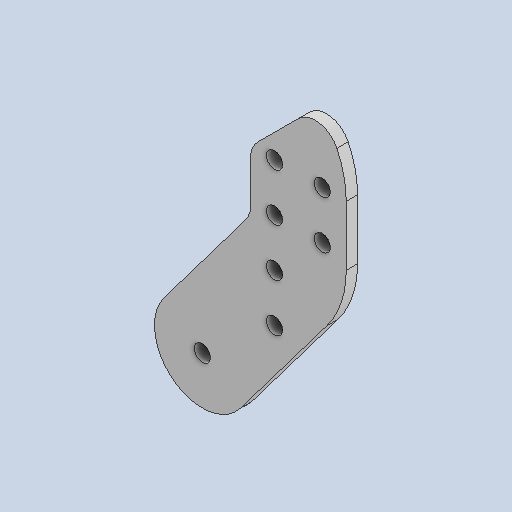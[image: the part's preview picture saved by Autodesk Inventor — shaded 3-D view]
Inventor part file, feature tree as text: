
AUTODESK INVENTOR PART (.ipt)
format: ipt  version: 2023 (Build 270158000, 158)  size: 117,248 bytes
history: native  units: in
note: dims shown in document units (in); Inventor stores cm internally (conversion verified against a paired STEP export)
features: other x3, sketch x1
ambient origin geometry x8: Origin, YZ Plane, XZ Plane, XY Plane, X Axis, Y Axis, Z Axis, Center Point
bodies: Solid1 (feature_tree)
feature tree (4):
  other  "IntakeAftArm.ipt"
  other  "Solid1::IntakeAftArm.ipt"
  other  "TaggingFeature1"
  sketch  "Sketch1"  dims[d0=0.3937in]
